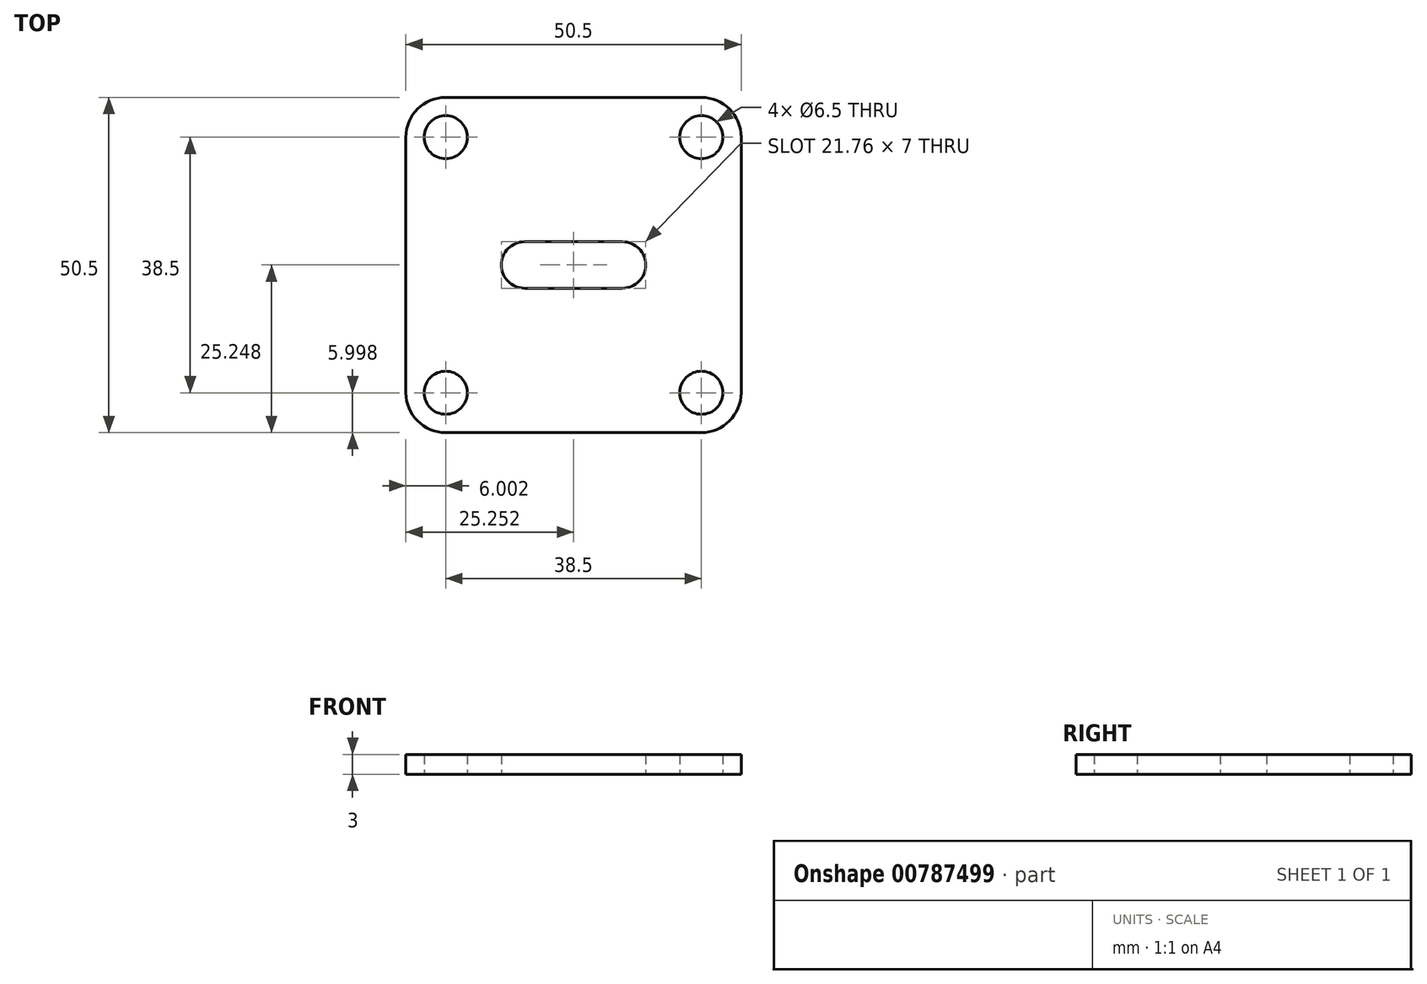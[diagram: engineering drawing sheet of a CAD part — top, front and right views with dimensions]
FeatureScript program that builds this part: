
annotation { "Feature Type Name" : "Feature", "Feature Type Description" : "" }
export const myFeature = defineFeature(function(context is Context, id is Id, definition is map)
    precondition{}
    {
        {
            var Q0;
            Q0=qCreatedBy(makeId("Top.planeOp"),FACE);
            var sketch = newSketch(context, id + "F0", { "sketchPlane" : qUnion([Q0])});
            skLineSegment(sketch, "E0.bottom", {"start": v(-18.05, 24.05) * mm, "end": v(20.45, 24.05) * mm});
            skLineSegment(sketch, "E0.top", {"start": v(-18.05, -26.45) * mm, "end": v(20.45, -26.45) * mm});
            skLineSegment(sketch, "E0.left", {"start": v(-24.05, 18.05) * mm, "end": v(-24.05, -20.45) * mm});
            skLineSegment(sketch, "E0.right", {"start": v(26.45, 18.05) * mm, "end": v(26.45, -20.45) * mm});
            skPoint(sketch, "E1.centerSnap0", {"position": v(1.2, 24.05) * mm});
            skPoint(sketch, "E1.centerSnap1", {"position": v(-24.05, -1.2) * mm});
            skPoint(sketch, "E2.visualSharp", {"position": v(-24.05, 24.05) * mm});
            skArc(sketch, "E2.filletArc", {"start": v(-18.05, 24.05) * mm, "mid": v(-22.3, 22.3) * mm, "end": v(-24.05, 18.05) * mm});
            skPoint(sketch, "E3.visualSharp", {"position": v(26.45, 24.05) * mm});
            skArc(sketch, "E3.filletArc", {"start": v(26.45, 18.05) * mm, "mid": v(24.7, 22.3) * mm, "end": v(20.45, 24.05) * mm});
            skPoint(sketch, "E4.visualSharp", {"position": v(26.45, -26.45) * mm});
            skArc(sketch, "E4.filletArc", {"start": v(20.45, -26.45) * mm, "mid": v(24.7, -24.7) * mm, "end": v(26.45, -20.45) * mm});
            skPoint(sketch, "E5.visualSharp", {"position": v(-24.05, -26.45) * mm});
            skArc(sketch, "E5.filletArc", {"start": v(-24.05, -20.45) * mm, "mid": v(-22.3, -24.7) * mm, "end": v(-18.05, -26.45) * mm});
            skCircle(sketch, "E6", {"center": v(-18.05, 18.05) * mm, "radius": 3.25 * mm});
            skCircle(sketch, "E7", {"center": v(20.45, 18.05) * mm, "radius": 3.25 * mm});
            skCircle(sketch, "E8", {"center": v(20.45, -20.45) * mm, "radius": 3.25 * mm});
            skCircle(sketch, "E9", {"center": v(-18.05, -20.45) * mm, "radius": 3.25 * mm});
            skArc(sketch, "E10", {"start": v(-6.18, 2.3) * mm, "mid": v(-9.68, -1.2) * mm, "end": v(-6.18, -4.7) * mm});
            skArc(sketch, "E11", {"start": v(8.58, -4.7) * mm, "mid": v(12.08, -1.2) * mm, "end": v(8.58, 2.3) * mm});
            skLineSegment(sketch, "E12", {"start": v(-6.18, 2.3) * mm, "end": v(8.58, 2.3) * mm});
            skLineSegment(sketch, "E13", {"start": v(8.58, -4.7) * mm, "end": v(-6.18, -4.7) * mm});
            skSolve(sketch);
        }
        {
            var Q0;
            Q0=makeQuery(id+"F0.imprint","IMPRINT",FACE,{"disambiguationData":[TD([[makeQuery(id+"F0.imprint","IMPRINT",EDGE,{"derivedFrom":sQuery(id+"F0.wireOp",EDGE,"E0.bottom")}),-1.0]])]});
            extrude(context, id + "F1", {"entities" : qUnion([Q0]), "depth" : 3 * mm, "offsetDistance" : 25.4 * mm});
        }
    });
